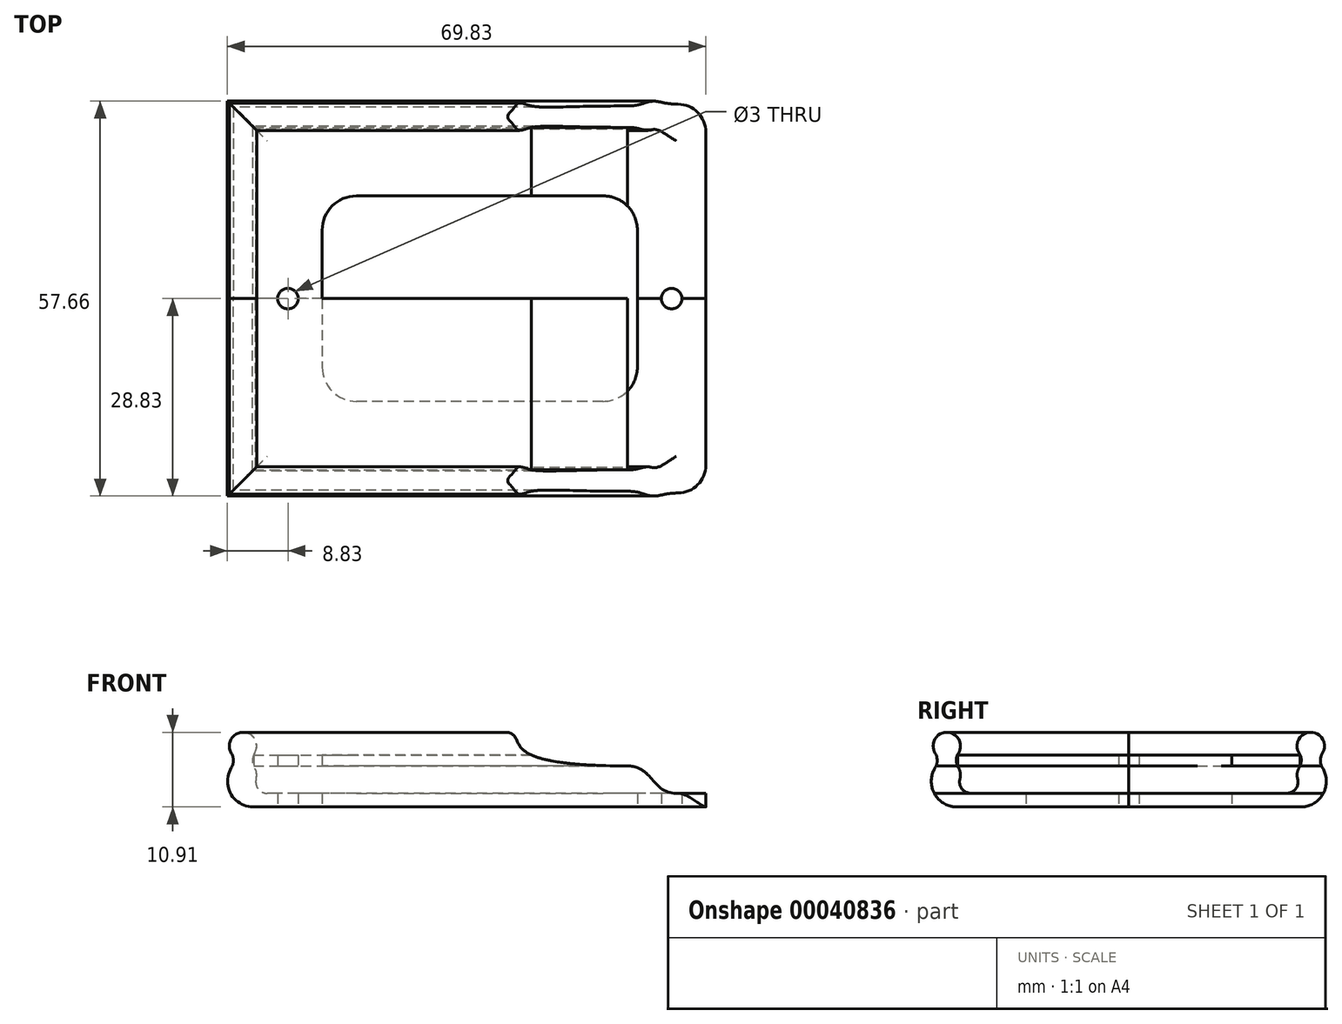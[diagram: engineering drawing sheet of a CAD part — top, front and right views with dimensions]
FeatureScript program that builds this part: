
annotation { "Feature Type Name" : "Feature", "Feature Type Description" : "" }
export const myFeature = defineFeature(function(context is Context, id is Id, definition is map)
    precondition{}
    {
        {
            var Q0;
            Q0=qCreatedBy(makeId("Right.planeOp"),FACE);
            var sketch = newSketch(context, id + "F0", { "sketchPlane" : qUnion([Q0])});
            skLineSegment(sketch, "E0.bottom", {"start": v(-25, 1.6) * mm, "end": v(25, 1.6) * mm});
            skLineSegment(sketch, "E0.top", {"start": v(-25, 0) * mm, "end": v(25, 0) * mm});
            skLineSegment(sketch, "E0.left", {"start": v(-25, 1.6) * mm, "end": v(-25, 0) * mm});
            skLineSegment(sketch, "E0.right", {"start": v(25, 1.6) * mm, "end": v(25, 0) * mm});
            skLineSegment(sketch, "E1", {"start": v(0, 0) * mm, "end": v(0, 1.6) * mm, "construction": true});
            skSolve(sketch);
        }
        {
            var Q0;
            Q0 = qSketchRegion(id + "F0", true);
            extrude(context, id + "F1", {"entities" : qUnion([Q0]), "oppositeDirection" : true, "depth" : 66 * mm});
        }
        {
            var Q0;
            Q0=makeQuery(id+"F1.opExtrude","SWEPT_FACE",FACE,{"disambiguationData":[OSD([sQuery(id+"F0.wireOp",EDGE,"E0.top")])]});
            var sketch = newSketch(context, id + "F2", { "sketchPlane" : qUnion([Q0])});
            skLineSegment(sketch, "E2", {"start": v(0, -25) * mm, "end": v(-66, -25) * mm});
            skLineSegment(sketch, "E3", {"start": v(-66, -25) * mm, "end": v(-66, 0) * mm});
            skSolve(sketch);
        }
        {
            var Q0;
            Q0=qCreatedBy(makeId("Right.planeOp"),FACE);
            var sketch = newSketch(context, id + "F3", { "sketchPlane" : qUnion([Q0])});
            skLineSegment(sketch, "E4", {"start": v(23.02, -4) * mm, "end": v(0, -4) * mm});
            skLineSegment(sketch, "E5", {"start": v(0, -4) * mm, "end": v(0, -6) * mm});
            skLineSegment(sketch, "E6", {"start": v(0, -6) * mm, "end": v(25.07, -6) * mm});
            skPoint(sketch, "E7.visualSharp", {"position": v(26.73, -6) * mm});
            skArc(sketch, "E7.filletArc", {"start": v(25.07, -6) * mm, "mid": v(28.36, -4.07) * mm, "end": v(28.26, -0.26) * mm});
            skArc(sketch, "E8", {"start": v(23.02, -4) * mm, "mid": v(24.37, -3.33) * mm, "end": v(24.64, -1.86) * mm});
            skPoint(sketch, "E9.orphan", {"position": v(27.88, -4) * mm});
            skArc(sketch, "E10", {"start": v(28.26, 1.86) * mm, "mid": v(26.56, 4.91) * mm, "end": v(24.87, 1.86) * mm});
            skLineSegment(sketch, "E11", {"start": v(26.56, 2.91) * mm, "end": v(26.56, -1.31) * mm, "construction": true});
            skArc(sketch, "E12", {"start": v(24.87, -0.26) * mm, "mid": v(25.17, 0.8) * mm, "end": v(24.87, 1.86) * mm});
            skArc(sketch, "E13", {"start": v(24.87, -0.26) * mm, "mid": v(24.58, -1.03) * mm, "end": v(24.64, -1.86) * mm});
            skArc(sketch, "E14.MirrorC", {"start": v(28.26, -0.26) * mm, "mid": v(27.96, 0.8) * mm, "end": v(28.26, 1.86) * mm});
            skSolve(sketch);
        }
        {
            var Q0;
            Q0 = qSketchRegion(id + "F3", true);
            var Q1;
            Q1 = qConstructionFilter(qBodyType(qCreatedBy(id + "F2" ,EDGE), BodyType.WIRE), ConstructionObject.NO);
            sweep(context, id + "F4", {"profiles" : qUnion([Q0]), "path" : qUnion([Q1])});
        }
        {
            var Q0;
            Q0=makeQuery(id+"F4.opSweep","SWEPT_FACE",FACE,{"disambiguationData":[OSD([sQuery(id+"F2.wireOp",EDGE,"E2"),sQuery(id+"F3.wireOp",EDGE,"E6")])]});
            var sketch = newSketch(context, id + "F5", { "sketchPlane" : qUnion([Q0])});
            skLineSegment(sketch, "E15.bottom", {"start": v(-10, 0) * mm, "end": v(-56, 0) * mm});
            skLineSegment(sketch, "E15.top", {"start": v(-15, -15) * mm, "end": v(-51, -15) * mm});
            skLineSegment(sketch, "E15.left", {"start": v(-10, 0) * mm, "end": v(-10, -10) * mm});
            skLineSegment(sketch, "E15.right", {"start": v(-56, 0) * mm, "end": v(-56, -10) * mm});
            skPoint(sketch, "E16.visualSharp", {"position": v(-10, -15) * mm});
            skArc(sketch, "E16.filletArc", {"start": v(-15, -15) * mm, "mid": v(-11.46, -13.54) * mm, "end": v(-10, -10) * mm});
            skPoint(sketch, "E17.visualSharp", {"position": v(-56, -15) * mm});
            skArc(sketch, "E17.filletArc", {"start": v(-56, -10) * mm, "mid": v(-54.54, -13.54) * mm, "end": v(-51, -15) * mm});
            skCircle(sketch, "E18", {"center": v(-5, 0) * mm, "radius": 1.5 * mm});
            skCircle(sketch, "E19", {"center": v(-61, 0) * mm, "radius": 1.5 * mm});
            skArc(sketch, "E20", {"start": v(-4.09, -28.4) * mm, "mid": v(-1.2, -27.2) * mm, "end": v(0, -24.3) * mm});
            skLineSegment(sketch, "E21", {"start": v(0, -24.3) * mm, "end": v(4.51, -24.3) * mm});
            skLineSegment(sketch, "E22", {"start": v(4.51, -24.3) * mm, "end": v(4.51, -29.67) * mm});
            skLineSegment(sketch, "E23", {"start": v(4.51, -29.67) * mm, "end": v(-4.09, -29.67) * mm});
            skLineSegment(sketch, "E24", {"start": v(-4.09, -29.67) * mm, "end": v(-4.09, -28.4) * mm});
            skSolve(sketch);
        }
        {
            var Q0;
            Q0 = qSketchRegion(id + "F5", true);
            extrude(context, id + "F6", {"entities" : qUnion([Q0]), "operationType" : NewBodyOperationType.REMOVE, "oppositeDirection" : true, "depth" : 25 * mm});
        }
        {
            var Q0;
            Q0=makeQuery(id+"F4.opSweep","SWEPT_BODY",BODY,{"disambiguationData":[OSD([sQuery(id+"F2.wireOp",EDGE,"E3"),sQuery(id+"F3.wireOp",EDGE,"E4"),sQuery(id+"F3.wireOp",EDGE,"E5"),sQuery(id+"F3.wireOp",EDGE,"E6"),sQuery(id+"F3.wireOp",EDGE,"E7.filletArc"),sQuery(id+"F3.wireOp",EDGE,"f8930a75-4973-4cff-9684-1931a1d01a80"),sQuery(id+"F3.wireOp",EDGE,"0626a36e-700c-46d1-b122-d66445e0e093"),sQuery(id+"F3.wireOp",EDGE,"E8"),sQuery(id+"F3.wireOp",EDGE,"de56b68e-5941-4569-9af6-f82dc7b3c43b0.MirrorCS"),sQuery(id+"F3.wireOp",EDGE,"a71f4e15-836c-4e19-a394-fad66be7ce71"),sQuery(id+"F3.wireOp",EDGE,"966170f1-62c2-4a59-a68a-9a5bb39e1a2e0.MirrorCS"),sQuery(id+"F3.wireOp",EDGE,"ddf0de8e-7826-47ad-b513-d74be3a71afb0.MirrorCS")])]});
            var Q1;
            Q1=qCreatedBy(makeId("Front.planeOp"),FACE);
            mirror(context, id + "F7", {"operationType" : NewBodyOperationType.ADD, "entities" : qUnion([Q0]), "mirrorPlane" : qUnion([Q1])});
        }
        {
            var Q0;
            Q0=qCreatedBy(makeId("Front.planeOp"),FACE);
            var sketch = newSketch(context, id + "F8", { "sketchPlane" : qUnion([Q0])});
            skLineSegment(sketch, "E25", {"start": v(-30, 5) * mm, "end": v(9.24, 5) * mm});
            skFitSpline(sketch, "E26", {"points": [v(-30, 5) * mm, v(-11.43, 0) * mm], "startDerivative": vector(16.41, 0) * mm, "endDerivative": vector(65.27, 0) * mm});
            skLineSegment(sketch, "E27", {"start": v(-4.33, -4) * mm, "end": v(9.24, -4) * mm});
            skLineSegment(sketch, "E28", {"start": v(9.24, -4) * mm, "end": v(9.24, 5) * mm});
            skLineSegment(sketch, "E29", {"start": v(-11.43, 0) * mm, "end": v(-29.99, 0) * mm, "construction": true});
            skFitSpline(sketch, "E30", {"points": [v(-11.43, 0) * mm, v(-4.33, -4) * mm], "startDerivative": vector(10.98, 0) * mm, "endDerivative": vector(10.43, 0) * mm});
            skSolve(sketch);
        }
        {
            var Q0;
            Q0 = qSketchRegion(id + "F8", true);
            extrude(context, id + "F9", {"entities" : qUnion([Q0]), "operationType" : NewBodyOperationType.REMOVE, "endBound" : BoundingType.SYMMETRIC, "oppositeDirection" : true, "depth" : 500 * mm});
        }
    });
